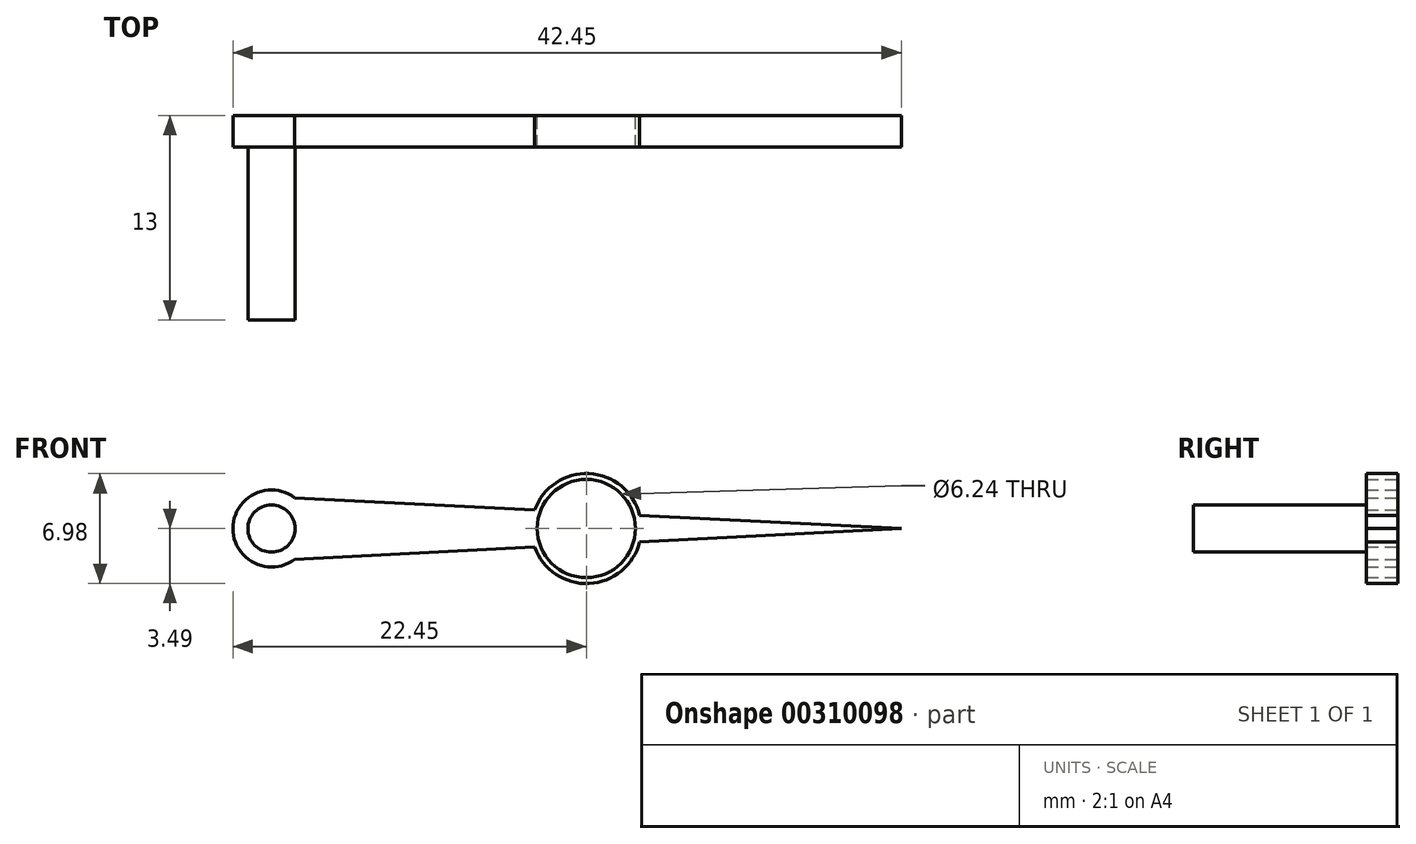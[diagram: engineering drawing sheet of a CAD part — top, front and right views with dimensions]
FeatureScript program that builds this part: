
annotation { "Feature Type Name" : "Feature", "Feature Type Description" : "" }
export const myFeature = defineFeature(function(context is Context, id is Id, definition is map)
    precondition{}
    {
        {
            var Q0;
            Q0=qCreatedBy(makeId("Front.planeOp"),FACE);
            var sketch = newSketch(context, id + "F0", { "sketchPlane" : qUnion([Q0])});
            skCircle(sketch, "E0", {"center": v(0, 0) * mm, "radius": 2.45 * mm});
            skLineSegment(sketch, "E1", {"start": v(0, 0) * mm, "end": v(40, 0) * mm, "construction": true});
            skLineSegment(sketch, "E2", {"start": v(1.48, 2.87) * mm, "end": v(1.48, -3.52) * mm, "construction": true});
            skLineSegment(sketch, "E3", {"start": v(1.48, 1.96) * mm, "end": v(16.71, 1.18) * mm});
            skLineSegment(sketch, "E4", {"start": v(40, 0) * mm, "end": v(23.39, -0.84) * mm});
            skCircle(sketch, "E5", {"center": v(20, 0) * mm, "radius": 3.5 * mm});
            skLineSegment(sketch, "E6.trimOffspring", {"start": v(23.39, 0.84) * mm, "end": v(40, 0) * mm});
            skLineSegment(sketch, "E7.trimOffspring", {"start": v(16.71, -1.18) * mm, "end": v(1.48, -1.96) * mm});
            skCircle(sketch, "E8", {"center": v(20, 0) * mm, "radius": 3.12 * mm});
            skSolve(sketch);
        }
        {
            var Q0;
            {var subQ0=sQuery(id+"F0.wireOp",EDGE,"E0");var subQ1=makeQuery(id+"F0.imprint","INTERSECT",VERTEX,{"derivedFrom":[subQ0,sQuery(id+"F0.wireOp",EDGE,"E3")]});Q0=makeQuery(id+"F0.imprint","IMPRINT",FACE,{"disambiguationData":[TD([[makeQuery(id+"F0.imprint","IMPRINT",EDGE,{"disambiguationData":[TD([[subQ1,-1.0]])],"derivedFrom":subQ0}),1.0]])]});}
            var Q1;
            {var subQ0=sQuery(id+"F0.wireOp",EDGE,"E3");Q1=makeQuery(id+"F0.imprint","IMPRINT",FACE,{"disambiguationData":[TD([[makeQuery(id+"F0.imprint","IMPRINT",EDGE,{"derivedFrom":subQ0}),-1.0]])]});}
            var Q2;
            {var subQ0=sQuery(id+"F0.wireOp",EDGE,"E5");var subQ1=makeQuery(id+"F0.imprint","INTERSECT",VERTEX,{"derivedFrom":[sQuery(id+"F0.wireOp",EDGE,"E3"),subQ0]});Q2=makeQuery(id+"F0.imprint","IMPRINT",FACE,{"disambiguationData":[TD([[makeQuery(id+"F0.imprint","IMPRINT",EDGE,{"disambiguationData":[TD([[subQ1,1.0]])],"derivedFrom":subQ0}),1.0]])]});}
            var Q3;
            {var subQ0=sQuery(id+"F0.wireOp",EDGE,"E4");Q3=makeQuery(id+"F0.imprint","IMPRINT",FACE,{"disambiguationData":[TD([[makeQuery(id+"F0.imprint","IMPRINT",EDGE,{"derivedFrom":subQ0}),-1.0]])]});}
            extrude(context, id + "F1", {"entities" : qUnion([Q0, Q1, Q2, Q3]), "endBound" : BoundingType.SYMMETRIC, "depth" : 2 * mm});
        }
        {
            var Q0;
            Q0=makeQuery(id+"F1.opExtrude","CAP_FACE",FACE,{"disambiguationData":[OSD([sQuery(id+"F0.wireOp",EDGE,"E0"),sQuery(id+"F0.wireOp",EDGE,"E3"),sQuery(id+"F0.wireOp",EDGE,"E4"),sQuery(id+"F0.wireOp",EDGE,"E5"),sQuery(id+"F0.wireOp",EDGE,"E6.trimOffspring"),sQuery(id+"F0.wireOp",EDGE,"E7.trimOffspring"),sQuery(id+"F0.wireOp",EDGE,"E8")])],"isStart":true});
            var sketch = newSketch(context, id + "F2", { "sketchPlane" : qUnion([Q0])});
            skCircle(sketch, "E9", {"center": v(0, 0) * mm, "radius": 1.5 * mm});
            skSolve(sketch);
        }
        {
            var Q0;
            Q0=makeQuery(id+"F2.imprint","IMPRINT",FACE,{"disambiguationData":[TD([[makeQuery(id+"F2.imprint","IMPRINT",EDGE,{"derivedFrom":sQuery(id+"F2.wireOp",EDGE,"E9")}),1.0]])]});
            extrude(context, id + "F3", {"entities" : qUnion([Q0]), "operationType" : NewBodyOperationType.ADD, "oppositeDirection" : true, "depth" : 13 * mm});
        }
    });
